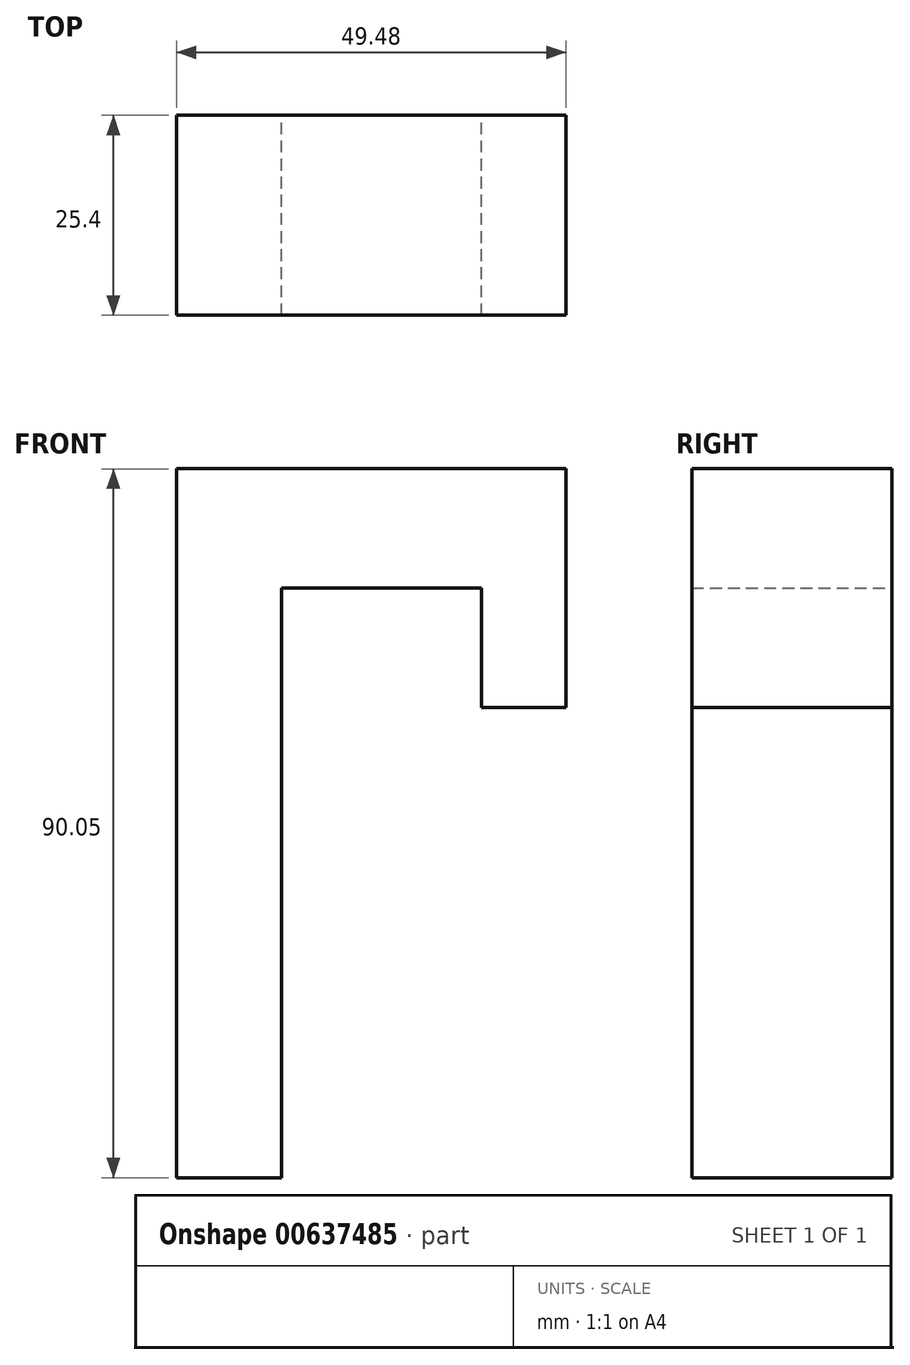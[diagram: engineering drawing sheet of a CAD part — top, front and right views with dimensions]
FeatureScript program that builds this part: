
annotation { "Feature Type Name" : "Feature", "Feature Type Description" : "" }
export const myFeature = defineFeature(function(context is Context, id is Id, definition is map)
    precondition{}
    {
        {
            var Q0;
            Q0=qCreatedBy(makeId("Front.planeOp"),FACE);
            var sketch = newSketch(context, id + "F0", { "sketchPlane" : qUnion([Q0])});
            skLineSegment(sketch, "E0", {"start": v(-101.42, 43.91) * mm, "end": v(-101.42, -46.14) * mm});
            skLineSegment(sketch, "E1", {"start": v(-101.42, -46.14) * mm, "end": v(-88.05, -46.14) * mm});
            skLineSegment(sketch, "E2", {"start": v(-88.05, -46.14) * mm, "end": v(-88.05, 28.76) * mm});
            skLineSegment(sketch, "E3", {"start": v(-88.05, 28.76) * mm, "end": v(-62.64, 28.76) * mm});
            skLineSegment(sketch, "E4", {"start": v(-62.64, 28.76) * mm, "end": v(-62.64, 13.6) * mm});
            skLineSegment(sketch, "E5", {"start": v(-62.64, 13.6) * mm, "end": v(-51.94, 13.6) * mm});
            skLineSegment(sketch, "E6", {"start": v(-51.94, 13.6) * mm, "end": v(-51.94, 43.91) * mm});
            skLineSegment(sketch, "E7", {"start": v(-51.94, 43.91) * mm, "end": v(-101.42, 43.91) * mm});
            skSolve(sketch);
        }
        {
            var Q0;
            Q0 = qSketchRegion(id + "F0", true);
            extrude(context, id + "F1", {"entities" : qUnion([Q0]), "depth" : 25.4 * mm, "offsetDistance" : 25.4 * mm});
        }
    });
